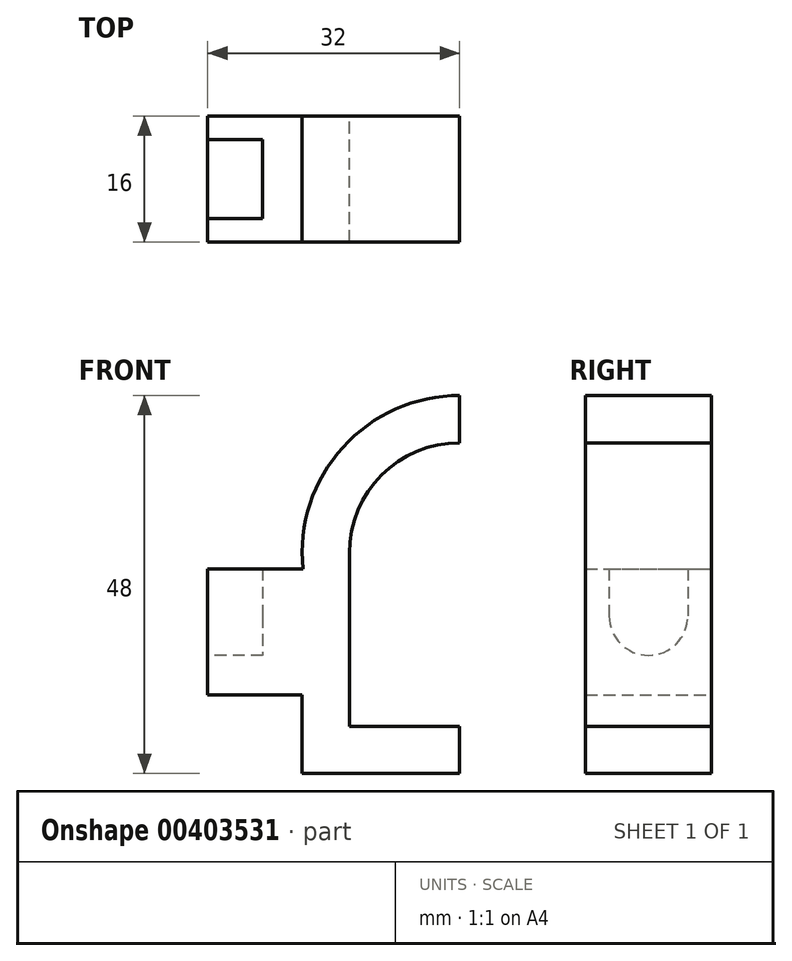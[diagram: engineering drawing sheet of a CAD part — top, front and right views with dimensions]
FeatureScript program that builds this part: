
annotation { "Feature Type Name" : "Feature", "Feature Type Description" : "" }
export const myFeature = defineFeature(function(context is Context, id is Id, definition is map)
    precondition{}
    {
        {
            var Q0;
            Q0=qCreatedBy(makeId("Front.planeOp"),FACE);
            var sketch = newSketch(context, id + "F0", { "sketchPlane" : qUnion([Q0])});
            skLineSegment(sketch, "E0", {"start": v(0, 0) * mm, "end": v(-20, 0) * mm});
            skLineSegment(sketch, "E1", {"start": v(0, 0) * mm, "end": v(0, 28) * mm, "construction": true});
            skLineSegment(sketch, "E2", {"start": v(-20, 0) * mm, "end": v(-20, 10) * mm});
            skLineSegment(sketch, "E3", {"start": v(-20, 10) * mm, "end": v(-32, 10) * mm});
            skLineSegment(sketch, "E4", {"start": v(-32, 10) * mm, "end": v(-32, 26) * mm});
            skArc(sketch, "E5", {"start": v(0, 48) * mm, "mid": v(-14.83, 41.42) * mm, "end": v(-19.9, 26) * mm});
            skLineSegment(sketch, "E6", {"start": v(-32, 26) * mm, "end": v(-19.9, 26) * mm});
            skArc(sketch, "E7.0", {"start": v(0, 42) * mm, "mid": v(-9.9, 37.9) * mm, "end": v(-14, 28) * mm});
            skLineSegment(sketch, "E8.0", {"start": v(-14, 6) * mm, "end": v(-14, 28) * mm});
            skLineSegment(sketch, "E8.1", {"start": v(0, 6) * mm, "end": v(-14, 6) * mm});
            skLineSegment(sketch, "E9", {"start": v(0, 48) * mm, "end": v(0, 42) * mm});
            skLineSegment(sketch, "E10", {"start": v(0, 6) * mm, "end": v(0, 0) * mm});
            skSolve(sketch);
        }
        {
            var Q0;
            Q0 = qSketchRegion(id + "F0", true);
            extrude(context, id + "F1", {"entities" : qUnion([Q0]), "depth" : 16 * mm});
        }
        {
            var Q0;
            Q0=makeQuery(id+"F1.opExtrude","SWEPT_FACE",FACE,{"disambiguationData":[OSD([sQuery(id+"F0.wireOp",EDGE,"E4")])]});
            var sketch = newSketch(context, id + "F2", { "sketchPlane" : qUnion([Q0])});
            skLineSegment(sketch, "E11.bottom", {"start": v(3, 26) * mm, "end": v(13, 26) * mm});
            skLineSegment(sketch, "E11.left", {"start": v(3, 26) * mm, "end": v(3, 20) * mm});
            skLineSegment(sketch, "E11.right", {"start": v(13, 26) * mm, "end": v(13, 20) * mm});
            skArc(sketch, "E12", {"start": v(3, 20) * mm, "mid": v(8, 15) * mm, "end": v(13, 20) * mm});
            skSolve(sketch);
        }
        {
            var Q0;
            Q0 = qSketchRegion(id + "F2", true);
            extrude(context, id + "F3", {"entities" : qUnion([Q0]), "operationType" : NewBodyOperationType.REMOVE, "oppositeDirection" : true, "depth" : ((64 - 40) / 2) * mm - 5 * mm});
        }
    });
